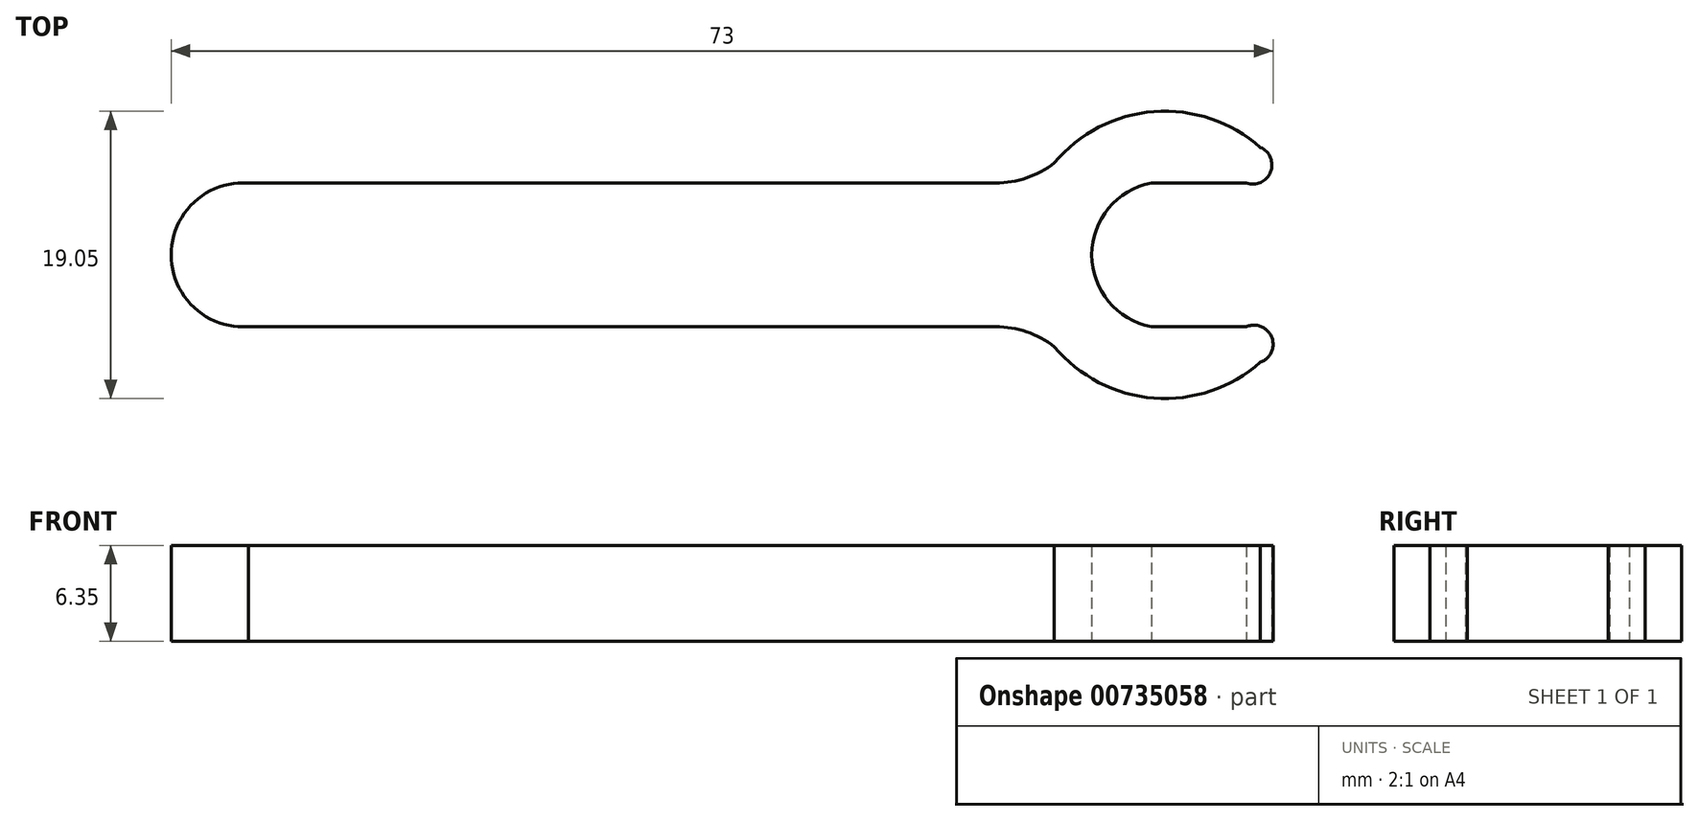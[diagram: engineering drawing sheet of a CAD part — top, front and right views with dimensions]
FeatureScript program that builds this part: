
annotation { "Feature Type Name" : "Feature", "Feature Type Description" : "" }
export const myFeature = defineFeature(function(context is Context, id is Id, definition is map)
    precondition{}
    {
        {
            var Q0;
            Q0=qCreatedBy(makeId("Top.planeOp"),FACE);
            var sketch = newSketch(context, id + "F0", { "sketchPlane" : qUnion([Q0])});
            skLineSegment(sketch, "E0", {"start": v(0, 0) * mm, "end": v(63.5, 0) * mm, "construction": true});
            skLineSegment(sketch, "E1", {"start": v(0, 6.35) * mm, "end": v(49.5, 6.35) * mm});
            skLineSegment(sketch, "E2", {"start": v(0, -3.18) * mm, "end": v(49.5, -3.18) * mm});
            skArc(sketch, "E3", {"start": v(0, 6.35) * mm, "mid": v(-5.12, 1.58) * mm, "end": v(0, -3.18) * mm});
            skPoint(sketch, "E4.visualSharp", {"position": v(50.67, 6.35) * mm});
            skArc(sketch, "E4.filletArc", {"start": v(49.5, 6.35) * mm, "mid": v(51.55, 6.69) * mm, "end": v(53.38, 7.67) * mm});
            skPoint(sketch, "E5.visualSharp", {"position": v(50.57, -3.18) * mm});
            skArc(sketch, "E5.filletArc", {"start": v(53.38, -4.5) * mm, "mid": v(51.55, -3.52) * mm, "end": v(49.5, -3.18) * mm});
            skArc(sketch, "E6", {"start": v(53.38, -4.5) * mm, "mid": v(59.99, -7.91) * mm, "end": v(67.03, -5.54) * mm});
            skArc(sketch, "E7", {"start": v(67.03, 8.7) * mm, "mid": v(59.99, 11.08) * mm, "end": v(53.38, 7.67) * mm});
            skArc(sketch, "E8", {"start": v(66.1, 6.35) * mm, "mid": v(67.71, 7.08) * mm, "end": v(67.03, 8.7) * mm});
            skArc(sketch, "E9", {"start": v(67.03, -5.54) * mm, "mid": v(67.79, -3.88) * mm, "end": v(66.1, -3.18) * mm});
            skLineSegment(sketch, "E10", {"start": v(66.1, 6.35) * mm, "end": v(59.8, 6.35) * mm});
            skLineSegment(sketch, "E11", {"start": v(66.1, -3.18) * mm, "end": v(59.8, -3.18) * mm});
            skArc(sketch, "E12", {"start": v(59.8, 6.35) * mm, "mid": v(55.86, 1.58) * mm, "end": v(59.8, -3.18) * mm});
            skSolve(sketch);
        }
        {
            var Q0;
            Q0=makeQuery(id+"F0.imprint","IMPRINT",FACE,{"disambiguationData":[TD([[makeQuery(id+"F0.imprint","IMPRINT",EDGE,{"derivedFrom":sQuery(id+"F0.wireOp",EDGE,"E1")}),-1.0]])]});
            var sketch = newSketch(context, id + "F1", { "sketchPlane" : qUnion([Q0])});
            skSolve(sketch);
        }
        {
            var Q0;
            Q0=makeQuery(id+"F1.imprint","IMPRINT",FACE,{"disambiguationData":[TD([[makeQuery(id+"F1.imprint","IMPRINT",EDGE,{"derivedFrom":makeQuery(id+"F0.imprint","IMPRINT",EDGE,{"derivedFrom":sQuery(id+"F0.wireOp",EDGE,"E1")})}),-1.0]])]});
            extrude(context, id + "F2", {"entities" : qUnion([Q0]), "depth" : 6.35 * mm, "offsetDistance" : 25.4 * mm});
        }
    });
